# Revit family: TV-122_RFA
name_source: partatom
category: Aparatos sanitarios
units: mm (PartAtom-declared; Revit-internal decimal feet)

## family parameters
Compartido = Sí
Corte con vacíos al cargar = No
Cota de conector redondo = Diámetro de uso
Número OmniClass = 23.45.55.14
Punto de cálculo de habitación = Sí
Se basa en plano de trabajo = No
Siempre vertical = Sí
Tipo de pieza = Normal
Título OmniClass = Single Faucets

## types (1)
- TV-122
    Certification = http://www.helvex.com.mx
    Chrome = Brass Chromed
    Comentarios de tipo = Special Products
    Conexión AF = Sí
    Descripción = Timing Of Push Ouput
    Documentation = http://www.helvex.com.mx
    Elevación por Defecto = 1"
    Elevación por defecto = 0"
    Fabricante = Helvex
    Features = Adjustable Shut-off Timer
    Inlet Threads = ½" - 14 NPSM
    Instructive = http://www.helvex.com.mx
    Max. Working Pressure = 85.3 psi
    Min. Working Pressure = 14.2 psi
    Modelo = TV-122
    Satin = Brass Satin
    URL = http://www.helvex.com.mx

## geometry (parser evidence)
native form markers: Sweep x3
no freeform markers — native parametric forms only
